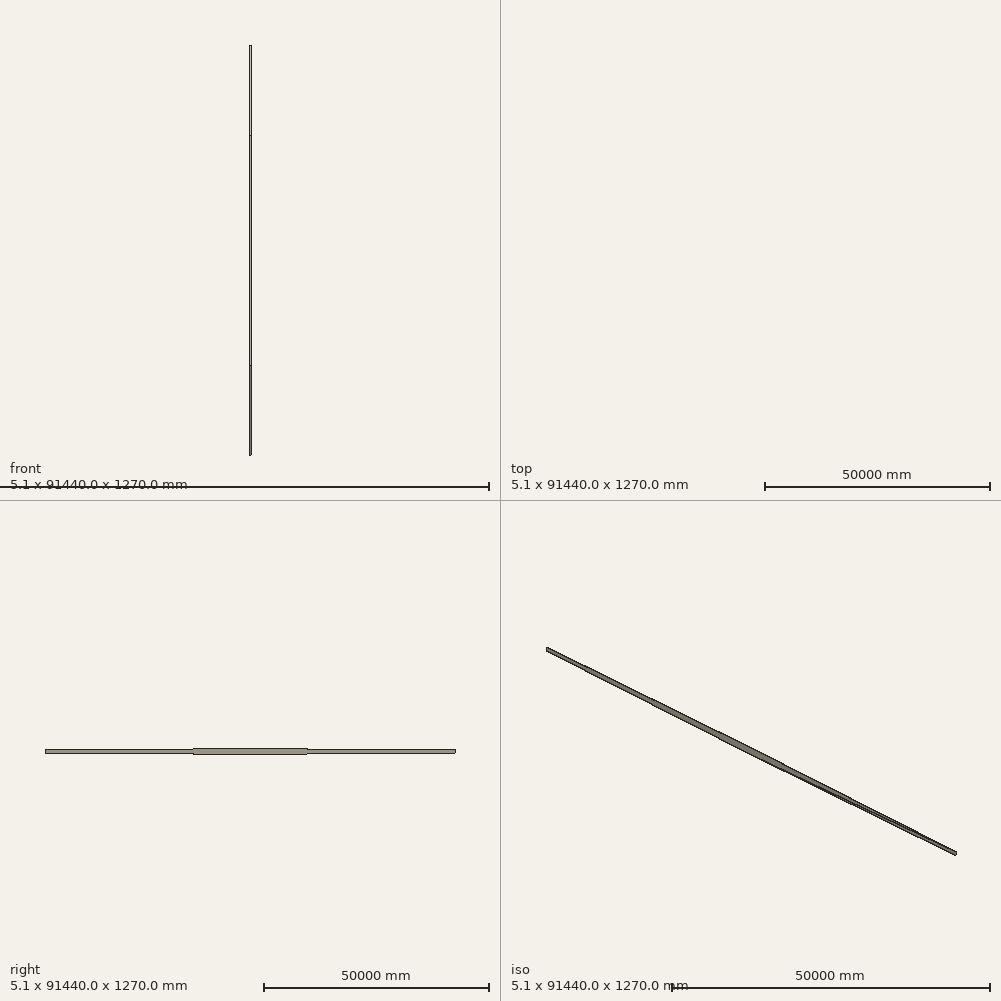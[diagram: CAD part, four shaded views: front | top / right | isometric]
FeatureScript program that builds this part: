
annotation { "Feature Type Name" : "Feature", "Feature Type Description" : "" }
export const myFeature = defineFeature(function(context is Context, id is Id, definition is map)
    precondition{}
    {
        {
            var Q0;
            Q0=qCreatedBy(makeId("Right.planeOp"),FACE);
            var sketch = newSketch(context, id + "F0", { "sketchPlane" : qUnion([Q0])});
            skLineSegment(sketch, "E0.left", {"start": v(0, 0) * mm, "end": v(0, 1270) * mm});
            skLineSegment(sketch, "E0.right", {"start": v(45720, 279.4) * mm, "end": v(45720, 990.6) * mm});
            skLineSegment(sketch, "E1", {"start": v(0, 0) * mm, "end": v(45720, 279.4) * mm});
            skLineSegment(sketch, "E2", {"start": v(45720, 990.6) * mm, "end": v(0, 1270) * mm});
            skLineSegment(sketch, "E3", {"start": v(0, 635) * mm, "end": v(1640.54, 635) * mm, "construction": true});
            skPoint(sketch, "E3.endSnap0", {"position": v(0, 635) * mm});
            skPoint(sketch, "E4", {"position": v(45720, 990.6) * mm});
            skPoint(sketch, "E5", {"position": v(45720, 279.4) * mm});
            skLineSegment(sketch, "E6.MirrorCS", {"start": v(-45720, 990.6) * mm, "end": v(0, 1270) * mm});
            skLineSegment(sketch, "E7.MirrorCS", {"start": v(0, 0) * mm, "end": v(-45720, 279.4) * mm});
            skLineSegment(sketch, "E8.MirrorCS", {"start": v(-45720, 279.4) * mm, "end": v(-45720, 990.6) * mm});
            skSolve(sketch);
        }
        {
            var Q0;
            Q0 = qSketchRegion(id + "F0", true);
            extrude(context, id + "F1", {"entities" : qUnion([Q0]), "depth" : 5.08 * mm, "offsetDistance" : 25.4 * mm});
        }
        {
            var Q0;
            Q0=makeQuery(id+"F1.opExtrude","SWEPT_BODY",BODY,{"disambiguationData":[OSD([sQuery(id+"F0.wireOp",EDGE,"E0.right"),sQuery(id+"F0.wireOp",EDGE,"E1"),sQuery(id+"F0.wireOp",EDGE,"E2"),sQuery(id+"F0.wireOp",EDGE,"E6.MirrorCS"),sQuery(id+"F0.wireOp",EDGE,"E7.MirrorCS"),sQuery(id+"F0.wireOp",EDGE,"E8.MirrorCS")])]});
            transform(context, id + "F2", {"entities" : qUnion([Q0]), "transformType" : TransformType.TRANSLATION_3D, "dx" : 0 * mm, "dy" : 0 * mm, "dz" : 0 * mm, "makeCopy" : true});
        }
    });
